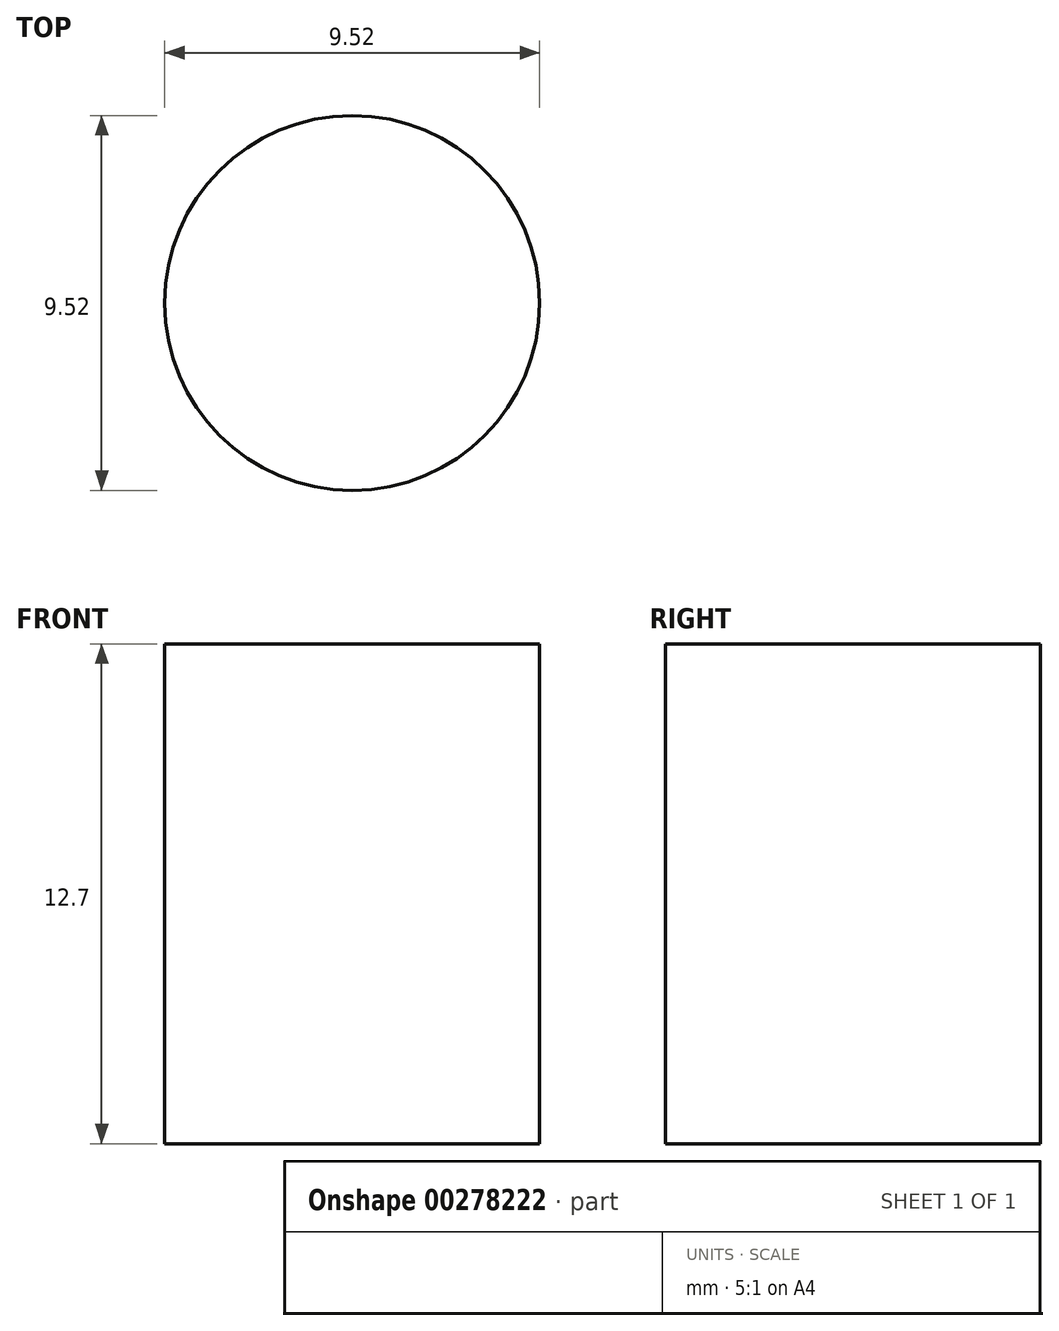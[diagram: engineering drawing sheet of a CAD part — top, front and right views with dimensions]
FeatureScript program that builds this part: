
annotation { "Feature Type Name" : "Feature", "Feature Type Description" : "" }
export const myFeature = defineFeature(function(context is Context, id is Id, definition is map)
    precondition{}
    {
        {
            var Q0;
            Q0=qCreatedBy(makeId("Top.planeOp"),FACE);
            var sketch = newSketch(context, id + "F0", { "sketchPlane" : qUnion([Q0])});
            skCircle(sketch, "E0", {"center": v(0, 0) * mm, "radius": 4.76 * mm});
            skSolve(sketch);
        }
        {
            var Q0;
            Q0=makeQuery(id+"F0.imprint","IMPRINT",FACE,{"disambiguationData":[TD([[makeQuery(id+"F0.imprint","IMPRINT",EDGE,{"derivedFrom":sQuery(id+"F0.wireOp",EDGE,"E0")}),1.0]])]});
            extrude(context, id + "F1", {"entities" : qUnion([Q0]), "depth" : 12.7 * mm});
        }
    });
